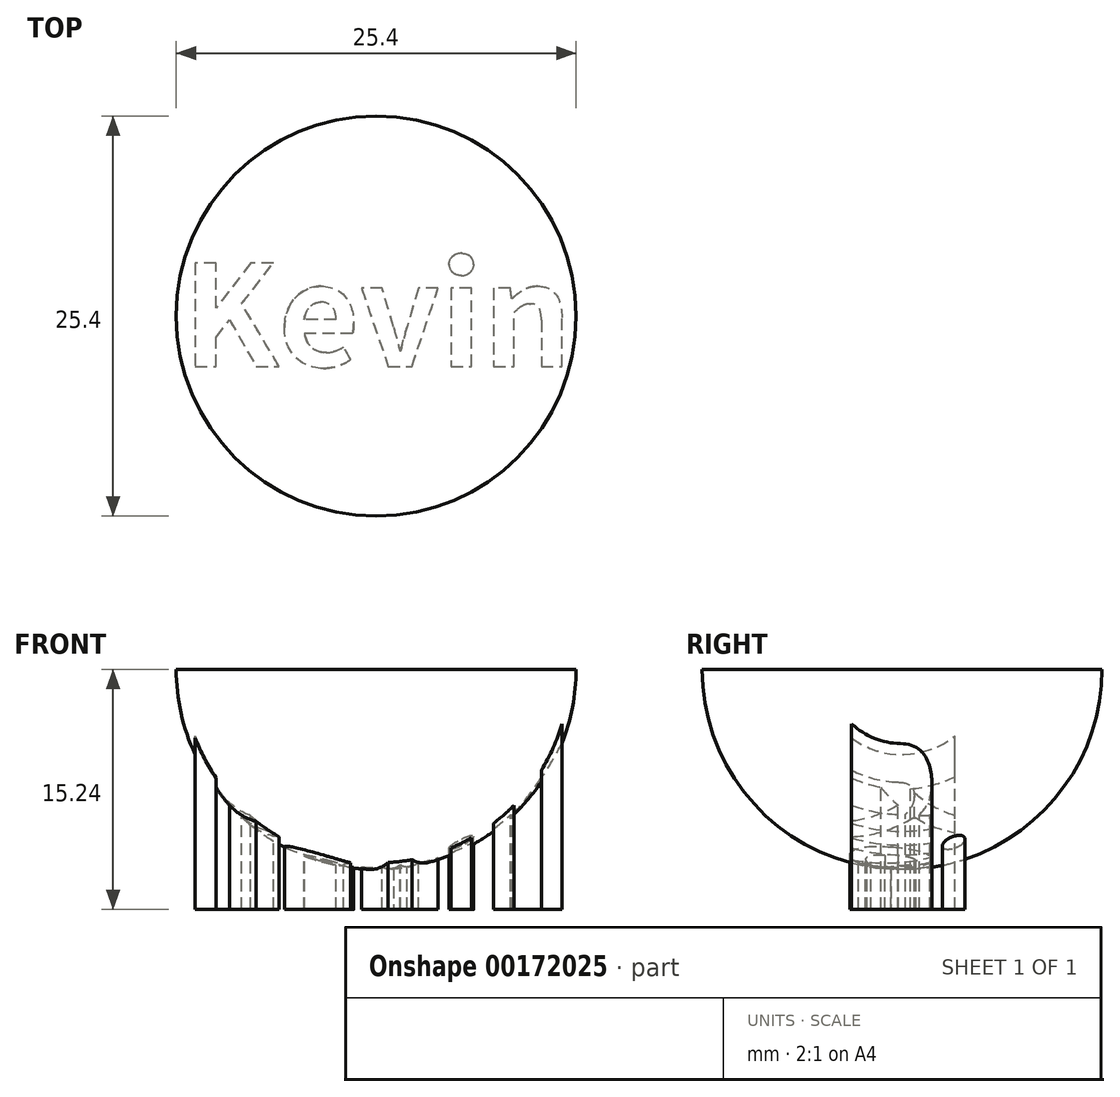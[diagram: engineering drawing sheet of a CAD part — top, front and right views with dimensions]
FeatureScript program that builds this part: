
annotation { "Feature Type Name" : "Feature", "Feature Type Description" : "" }
export const myFeature = defineFeature(function(context is Context, id is Id, definition is map)
    precondition{}
    {
        {
            var Q0;
            Q0=qCreatedBy(makeId("Top.planeOp"),FACE);
            var sketch = newSketch(context, id + "F0", { "sketchPlane" : qUnion([Q0])});
            skArc(sketch, "E0", {"start": v(-12.7, 0) * mm, "mid": v(0, -12.7) * mm, "end": v(12.7, 0) * mm});
            skLineSegment(sketch, "E1", {"start": v(-12.7, 0) * mm, "end": v(12.7, 0) * mm});
            skArc(sketch, "E2", {"start": v(-12.7, 0) * mm, "mid": v(0, 12.7) * mm, "end": v(12.7, 0) * mm});
            skSolve(sketch);
        }
        {
            var Q0;
            Q0=makeQuery(id+"F0.imprint","IMPRINT",FACE,{"disambiguationData":[TD([[makeQuery(id+"F0.imprint","IMPRINT",EDGE,{"derivedFrom":sQuery(id+"F0.wireOp",EDGE,"E1")}),1.0]])]});
            var sketch = newSketch(context, id + "F1", { "sketchPlane" : qUnion([Q0])});
            skText(sketch, "E3", { "text": "Kevin", "fontName": "NotoSansCJKsc-Bold.otf"});
            const initialGuessF1  = {"E3": [-0.0123, -0.0032, 1, 0, 0.00639]};
            skSetInitialGuess(sketch, initialGuessF1);
            skSolve(sketch);
        }
        {
            var Q0;
            Q0=makeQuery(id+"F0.imprint","IMPRINT",FACE,{"disambiguationData":[TD([[makeQuery(id+"F0.imprint","IMPRINT",EDGE,{"derivedFrom":sQuery(id+"F0.wireOp",EDGE,"E0")}),1.0]])]});
            var Q1;
            Q1=sQuery(id+"F0.wireOp",EDGE,"E0");
            var Q2;
            Q2=sQuery(id+"F0.wireOp",EDGE,"E1");
            revolve(context, id + "F2", {"entities" : qUnion([Q0]), "surfaceEntities" : qUnion([Q1]), "axis" : qUnion([Q2]), "revolveType" : RevolveType.ONE_DIRECTION, "angle" : 180 * degree});
        }
        {
            var Q0;
            Q0 = qSketchRegion(id + "F1", true);
            extrude(context, id + "F3", {"entities" : qUnion([Q0]), "operationType" : NewBodyOperationType.ADD, "oppositeDirection" : true, "depth" : 15.24 * mm});
        }
    });
